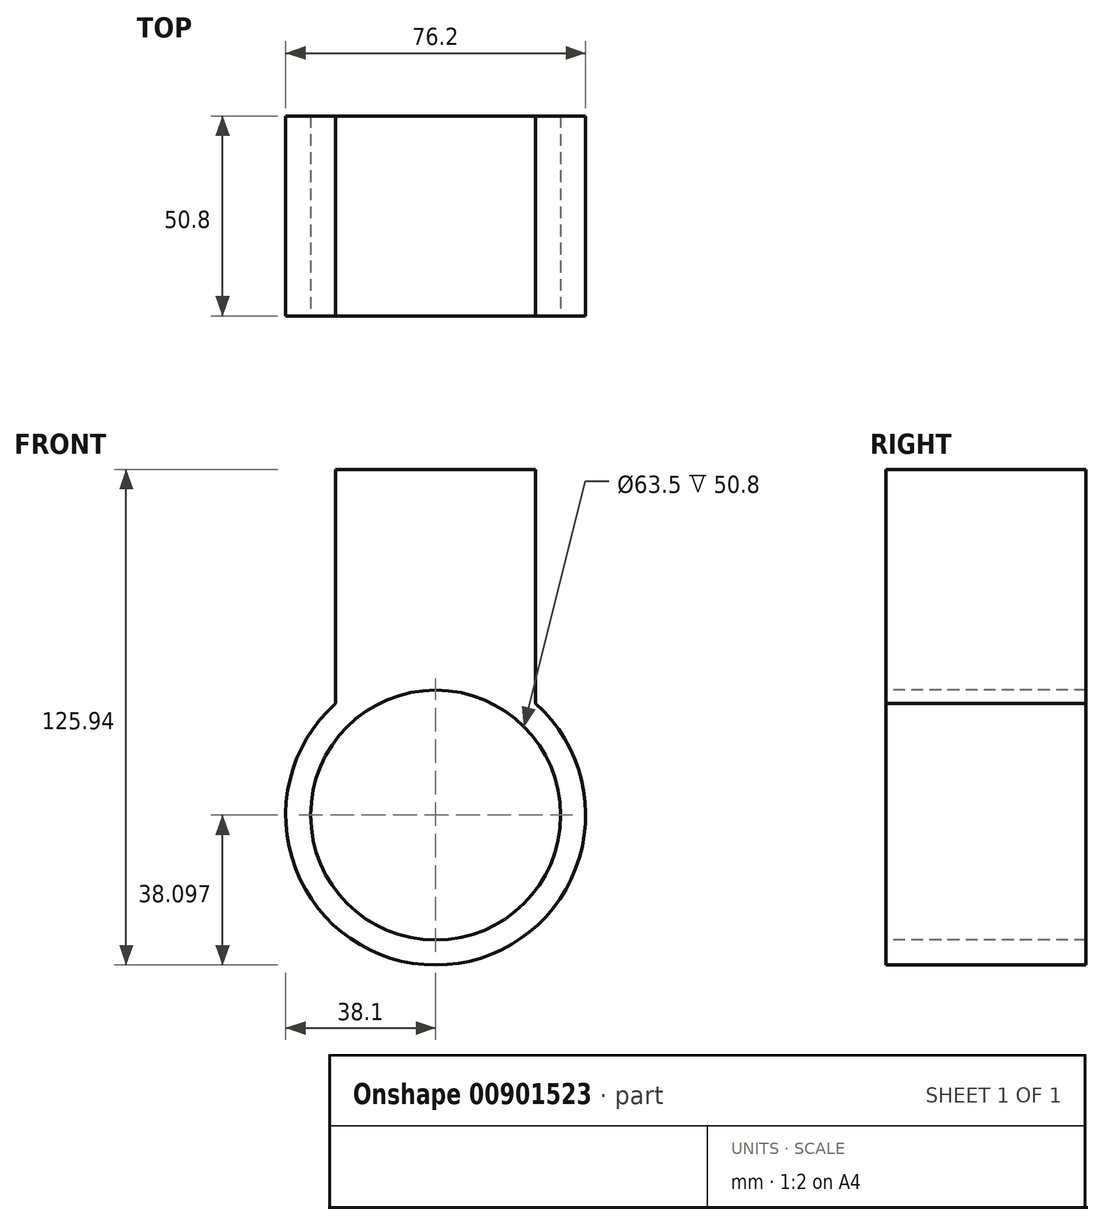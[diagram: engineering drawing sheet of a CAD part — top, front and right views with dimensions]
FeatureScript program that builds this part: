
annotation { "Feature Type Name" : "Feature", "Feature Type Description" : "" }
export const myFeature = defineFeature(function(context is Context, id is Id, definition is map)
    precondition{}
    {
        {
            var Q0;
            Q0=qCreatedBy(makeId("Front.planeOp"),FACE);
            var sketch = newSketch(context, id + "F0", { "sketchPlane" : qUnion([Q0])});
            skCircle(sketch, "E0", {"center": v(0, -59.2) * mm, "radius": 38.1 * mm});
            skLineSegment(sketch, "E1.bottom", {"start": v(-25.4, 28.65) * mm, "end": v(25.4, 28.65) * mm});
            skLineSegment(sketch, "E1.top", {"start": v(-25.4, -47.55) * mm, "end": v(25.4, -47.55) * mm});
            skLineSegment(sketch, "E1.left", {"start": v(-25.4, 28.65) * mm, "end": v(-25.4, -47.55) * mm});
            skLineSegment(sketch, "E1.right", {"start": v(25.4, 28.65) * mm, "end": v(25.4, -47.55) * mm});
            skSolve(sketch);
        }
        {
            var Q0;
            Q0 = qSketchRegion(id + "F0", true);
            extrude(context, id + "F1", {"entities" : qUnion([Q0]), "depth" : 50.8 * mm, "offsetDistance" : 25.4 * mm});
        }
        {
            var Q0;
            Q0=makeQuery(id+"F1.opExtrude","CAP_FACE",FACE,{"disambiguationData":[OSD([sQuery(id+"F0.wireOp",EDGE,"E0"),sQuery(id+"F0.wireOp",EDGE,"E1.bottom"),sQuery(id+"F0.wireOp",EDGE,"E1.left"),sQuery(id+"F0.wireOp",EDGE,"E1.right")])],"isStart":false});
            var sketch = newSketch(context, id + "F2", { "sketchPlane" : qUnion([Q0])});
            skCircle(sketch, "E2", {"center": v(0, -59.2) * mm, "radius": 31.57 * mm});
            skSolve(sketch);
        }
        {
            var Q0;
            Q0=sQuery(id+"F2.wireOp",VERTEX,"E2.center");
            var Q1;
            Q1=makeQuery(id+"F1.opExtrude","SWEPT_BODY",BODY,{"disambiguationData":[OSD([sQuery(id+"F0.wireOp",EDGE,"E0"),sQuery(id+"F0.wireOp",EDGE,"E1.bottom"),sQuery(id+"F0.wireOp",EDGE,"E1.left"),sQuery(id+"F0.wireOp",EDGE,"E1.right")])]});
            hole(context, id + "F3", {"style" : HoleStyle.SIMPLE, "endStyle" : HoleEndStyle.THROUGH, "holeDiameter" : 63.5 * mm, "majorDiameter" : 6.35 * mm, "isTappedThrough" : true, "tappedDepth" : 12.7 * mm, "tapClearance" : 3, "locations" : qUnion([Q0]), "scope" : qUnion([Q1])});
        }
    });
